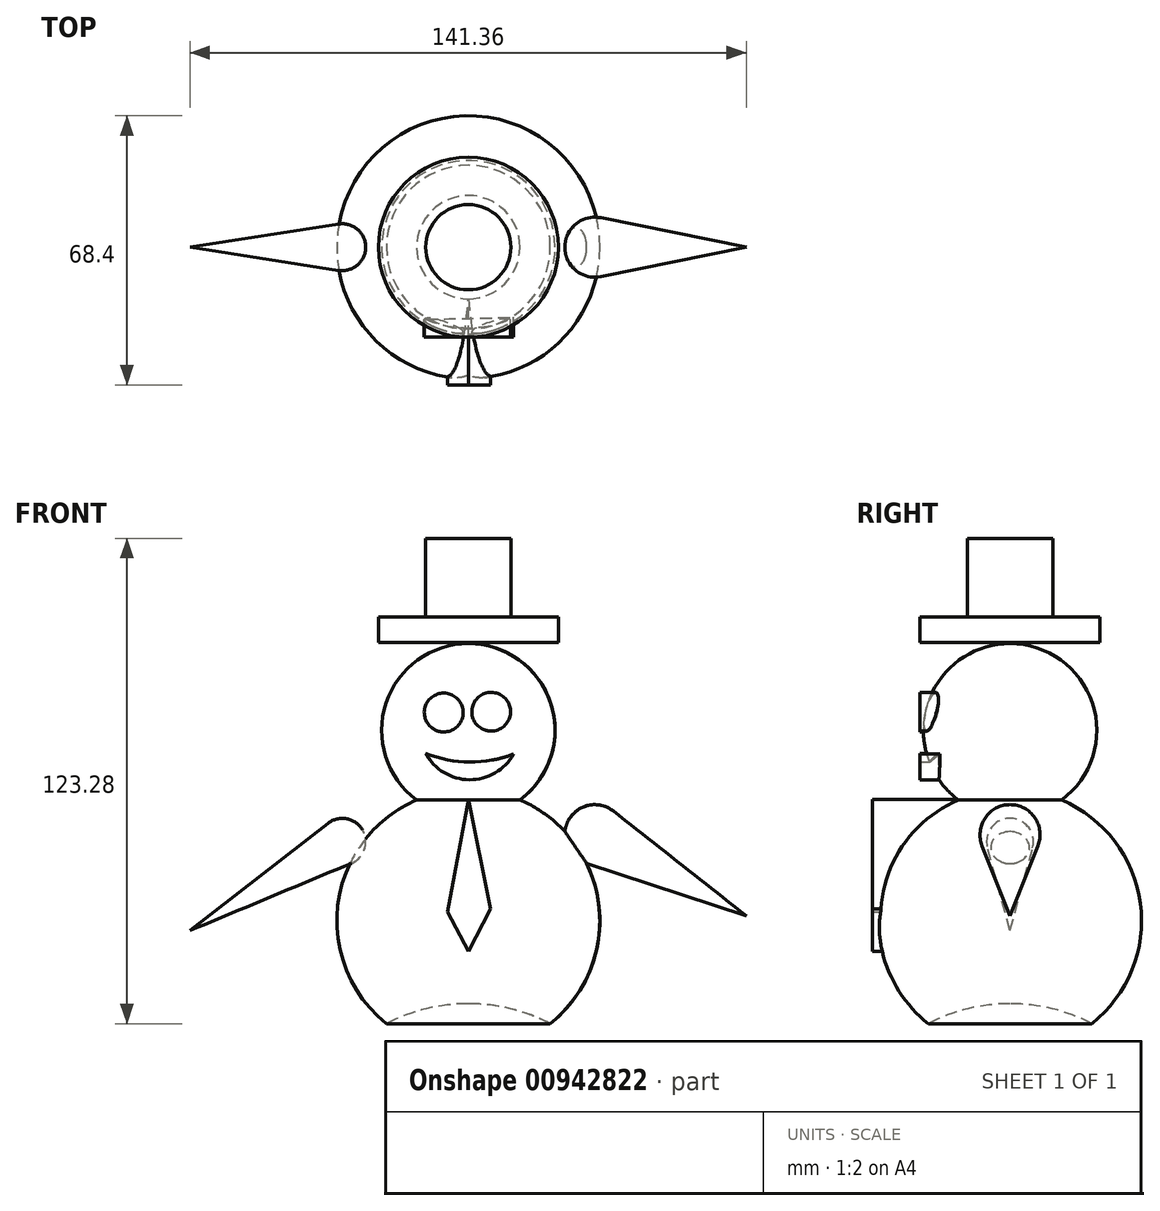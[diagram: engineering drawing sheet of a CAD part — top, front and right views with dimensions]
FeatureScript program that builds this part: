
annotation { "Feature Type Name" : "Feature", "Feature Type Description" : "" }
export const myFeature = defineFeature(function(context is Context, id is Id, definition is map)
    precondition{}
    {
        {
            var Q0;
            Q0=qCreatedBy(makeId("Front.planeOp"),FACE);
            var sketch = newSketch(context, id + "F0", { "sketchPlane" : qUnion([Q0])});
            skCircle(sketch, "E0", {"center": v(0, 56.18) * mm, "radius": 22.02 * mm});
            skCircle(sketch, "E1", {"center": v(0, 7.77) * mm, "radius": 33.4 * mm});
            skCircle(sketch, "E2", {"center": v(0, -58.54) * mm, "radius": 45.24 * mm});
            skLineSegment(sketch, "E3", {"start": v(0, 78.2) * mm, "end": v(0, -103.78) * mm});
            skSolve(sketch);
        }
        {
            var Q0;
            {var subQ0=sQuery(id+"F0.wireOp",EDGE,"E3");var subQ1=sQuery(id+"F0.wireOp",EDGE,"E0");var subQ2=makeQuery(id+"F0.imprint","INTERSECT",VERTEX,{"disambiguationData":[OD(0.0)],"derivedFrom":[subQ1,subQ0]});Q0=makeQuery(id+"F0.imprint","IMPRINT",FACE,{"disambiguationData":[TD([[makeQuery(id+"F0.imprint","IMPRINT",EDGE,{"disambiguationData":[TD([[subQ2,-1.0]])],"derivedFrom":subQ1}),1.0]])]});}
            var Q1;
            {var subQ0=sQuery(id+"F0.wireOp",EDGE,"E1");var subQ1=sQuery(id+"F0.wireOp",EDGE,"E0");var subQ2=makeQuery(id+"F0.imprint","INTERSECT",VERTEX,{"disambiguationData":[OD(0.0)],"derivedFrom":[subQ1,subQ0]});Q1=makeQuery(id+"F0.imprint","IMPRINT",FACE,{"disambiguationData":[TD([[makeQuery(id+"F0.imprint","IMPRINT",EDGE,{"disambiguationData":[TD([[subQ2,-1.0]])],"derivedFrom":subQ1}),1.0]])]});}
            var Q2;
            {var subQ0=sQuery(id+"F0.wireOp",EDGE,"E1");var subQ1=sQuery(id+"F0.wireOp",EDGE,"E0");var subQ2=makeQuery(id+"F0.imprint","INTERSECT",VERTEX,{"disambiguationData":[OD(0.0)],"derivedFrom":[subQ1,subQ0]});Q2=makeQuery(id+"F0.imprint","IMPRINT",FACE,{"disambiguationData":[TD([[makeQuery(id+"F0.imprint","IMPRINT",EDGE,{"disambiguationData":[TD([[subQ2,-1.0]])],"derivedFrom":subQ1}),-1.0]])]});}
            var Q3;
            {var subQ0=sQuery(id+"F0.wireOp",EDGE,"E2");var subQ1=sQuery(id+"F0.wireOp",EDGE,"E1");var subQ2=makeQuery(id+"F0.imprint","INTERSECT",VERTEX,{"disambiguationData":[OD(0.0)],"derivedFrom":[subQ1,subQ0]});Q3=makeQuery(id+"F0.imprint","IMPRINT",FACE,{"disambiguationData":[TD([[makeQuery(id+"F0.imprint","IMPRINT",EDGE,{"disambiguationData":[TD([[subQ2,-1.0]])],"derivedFrom":subQ1}),1.0]])]});}
            var Q4;
            {var subQ0=sQuery(id+"F0.wireOp",EDGE,"E2");var subQ1=sQuery(id+"F0.wireOp",EDGE,"E1");var subQ2=makeQuery(id+"F0.imprint","INTERSECT",VERTEX,{"disambiguationData":[OD(0.0)],"derivedFrom":[subQ1,subQ0]});Q4=makeQuery(id+"F0.imprint","IMPRINT",FACE,{"disambiguationData":[TD([[makeQuery(id+"F0.imprint","IMPRINT",EDGE,{"disambiguationData":[TD([[subQ2,-1.0]])],"derivedFrom":subQ1}),-1.0]])]});}
            var Q5;
            Q5=sQuery(id+"F0.wireOp",EDGE,"E3");
            revolve(context, id + "F1", {"surfaceOperationType" : NewSurfaceOperationType.NEW, "entities" : qUnion([Q0, Q1, Q2, Q3, Q4]), "axis" : qUnion([Q5]), "revolveType" : RevolveType.FULL});
        }
        {
            var Q0;
            Q0=qCreatedBy(makeId("Front.planeOp"),FACE);
            var sketch = newSketch(context, id + "F2", { "sketchPlane" : qUnion([Q0])});
            skCircle(sketch, "E4", {"center": v(-32.02, 27.86) * mm, "radius": 5.95 * mm});
            skLineSegment(sketch, "E5", {"start": v(-32.02, 27.86) * mm, "end": v(-70.74, 5.31) * mm});
            skLineSegment(sketch, "E6", {"start": v(-70.74, 5.31) * mm, "end": v(-35.66, 32.55) * mm});
            skLineSegment(sketch, "E7", {"start": v(-35.66, 32.55) * mm, "end": v(-32.02, 27.86) * mm});
            skLineSegment(sketch, "E8", {"start": v(-32.02, 27.86) * mm, "end": v(-26.87, 30.85) * mm});
            skSolve(sketch);
        }
        {
            var Q0;
            {var subQ0=sQuery(id+"F2.wireOp",EDGE,"E6");Q0=makeQuery(id+"F2.imprint","IMPRINT",FACE,{"disambiguationData":[TD([[makeQuery(id+"F2.imprint","IMPRINT",EDGE,{"derivedFrom":subQ0}),-1.0]])]});}
            var Q1;
            {var subQ0=sQuery(id+"F2.wireOp",EDGE,"E7");Q1=makeQuery(id+"F2.imprint","IMPRINT",FACE,{"disambiguationData":[TD([[makeQuery(id+"F2.imprint","IMPRINT",EDGE,{"derivedFrom":subQ0}),1.0]])]});}
            var Q2;
            {var subQ0=sQuery(id+"F2.wireOp",EDGE,"E7");Q2=makeQuery(id+"F2.imprint","IMPRINT",FACE,{"disambiguationData":[TD([[makeQuery(id+"F2.imprint","IMPRINT",EDGE,{"derivedFrom":subQ0}),-1.0]])]});}
            var Q3;
            Q3=sQuery(id+"F2.wireOp",EDGE,"E5");
            revolve(context, id + "F3", {"surfaceOperationType" : NewSurfaceOperationType.NEW, "entities" : qUnion([Q0, Q1, Q2]), "axis" : qUnion([Q3]), "revolveType" : RevolveType.FULL});
        }
        {
            var Q0;
            Q0=qCreatedBy(makeId("Front.planeOp"),FACE);
            var sketch = newSketch(context, id + "F4", { "sketchPlane" : qUnion([Q0])});
            skCircle(sketch, "E9", {"center": v(32.13, 29.65) * mm, "radius": 7.63 * mm});
            skLineSegment(sketch, "E10", {"start": v(32.13, 29.65) * mm, "end": v(70.62, 9.03) * mm});
            skLineSegment(sketch, "E11", {"start": v(70.62, 9.03) * mm, "end": v(36.86, 35.65) * mm});
            skLineSegment(sketch, "E12", {"start": v(36.86, 35.65) * mm, "end": v(32.13, 29.65) * mm});
            skLineSegment(sketch, "E13", {"start": v(32.13, 29.65) * mm, "end": v(25.4, 33.26) * mm});
            skSolve(sketch);
        }
        {
            var Q0;
            {var subQ0=sQuery(id+"F4.wireOp",EDGE,"E11");Q0=makeQuery(id+"F4.imprint","IMPRINT",FACE,{"disambiguationData":[TD([[makeQuery(id+"F4.imprint","IMPRINT",EDGE,{"derivedFrom":subQ0}),1.0]])]});}
            var Q1;
            {var subQ0=sQuery(id+"F4.wireOp",EDGE,"E12");Q1=makeQuery(id+"F4.imprint","IMPRINT",FACE,{"disambiguationData":[TD([[makeQuery(id+"F4.imprint","IMPRINT",EDGE,{"derivedFrom":subQ0}),-1.0]])]});}
            var Q2;
            {var subQ0=sQuery(id+"F4.wireOp",EDGE,"E12");Q2=makeQuery(id+"F4.imprint","IMPRINT",FACE,{"disambiguationData":[TD([[makeQuery(id+"F4.imprint","IMPRINT",EDGE,{"derivedFrom":subQ0}),1.0]])]});}
            var Q3;
            Q3=sQuery(id+"F4.wireOp",EDGE,"E10");
            revolve(context, id + "F5", {"operationType" : NewBodyOperationType.ADD, "surfaceOperationType" : NewSurfaceOperationType.NEW, "entities" : qUnion([Q0, Q1, Q2]), "axis" : qUnion([Q3]), "revolveType" : RevolveType.FULL});
        }
        {
            var Q0;
            Q0=qCreatedBy(makeId("Front.planeOp"),FACE);
            var sketch = newSketch(context, id + "F6", { "sketchPlane" : qUnion([Q0])});
            skCircle(sketch, "E14", {"center": v(-6.26, 60.69) * mm, "radius": 4.94 * mm});
            skCircle(sketch, "E15", {"center": v(5.8, 60.9) * mm, "radius": 4.92 * mm});
            skArc(sketch, "E16", {"start": v(-10.83, 50.33) * mm, "mid": v(0.29, 43.62) * mm, "end": v(11.5, 50.16) * mm});
            skArc(sketch, "E17", {"start": v(-10.83, 50.33) * mm, "mid": v(0.32, 48.1) * mm, "end": v(11.5, 50.16) * mm});
            skSolve(sketch);
        }
        {
            var Q0;
            Q0 = qSketchRegion(id + "F6", true);
            extrude(context, id + "F7", {"entities" : qUnion([Q0]), "operationType" : NewBodyOperationType.ADD, "depth" : 22.86 * mm, "offsetDistance" : 25.4 * mm});
        }
        {
            var Q0;
            Q0=qCreatedBy(makeId("Front.planeOp"),FACE);
            var sketch = newSketch(context, id + "F8", { "sketchPlane" : qUnion([Q0])});
            skLineSegment(sketch, "E18", {"start": v(0, 38.59) * mm, "end": v(0, 0) * mm});
            skLineSegment(sketch, "E19", {"start": v(0, 0) * mm, "end": v(-5.33, 10.06) * mm});
            skLineSegment(sketch, "E20", {"start": v(-5.33, 10.06) * mm, "end": v(0, 38.59) * mm});
            skLineSegment(sketch, "E21", {"start": v(0, 38.59) * mm, "end": v(5.67, 10.75) * mm});
            skLineSegment(sketch, "E22", {"start": v(5.67, 10.75) * mm, "end": v(0, 0) * mm});
            skSolve(sketch);
        }
        {
            var Q0;
            Q0 = qSketchRegion(id + "F8", true);
            extrude(context, id + "F9", {"entities" : qUnion([Q0]), "operationType" : NewBodyOperationType.ADD, "depth" : 35 * mm, "offsetDistance" : 25.4 * mm});
        }
        {
            var Q0;
            Q0=qCreatedBy(makeId("Front.planeOp"),FACE);
            var sketch = newSketch(context, id + "F10", { "sketchPlane" : qUnion([Q0])});
            skLineSegment(sketch, "E23", {"start": v(-10.83, 104.92) * mm, "end": v(-10.83, 84.98) * mm});
            skLineSegment(sketch, "E24", {"start": v(-10.83, 84.98) * mm, "end": v(-22.85, 84.98) * mm});
            skLineSegment(sketch, "E25", {"start": v(-22.85, 84.98) * mm, "end": v(-22.85, 78.45) * mm});
            skLineSegment(sketch, "E26", {"start": v(-22.85, 78.45) * mm, "end": v(0, 78.45) * mm});
            skLineSegment(sketch, "E27", {"start": v(0, 78.45) * mm, "end": v(0, 104.92) * mm});
            skLineSegment(sketch, "E28", {"start": v(0, 104.92) * mm, "end": v(-10.83, 104.92) * mm});
            skSolve(sketch);
        }
        {
            var Q0;
            Q0 = qSketchRegion(id + "F10", true);
            var Q1;
            Q1=sQuery(id+"F10.wireOp",EDGE,"E27");
            revolve(context, id + "F11", {"surfaceOperationType" : NewSurfaceOperationType.NEW, "entities" : qUnion([Q0]), "axis" : qUnion([Q1]), "revolveType" : RevolveType.FULL});
        }
    });
